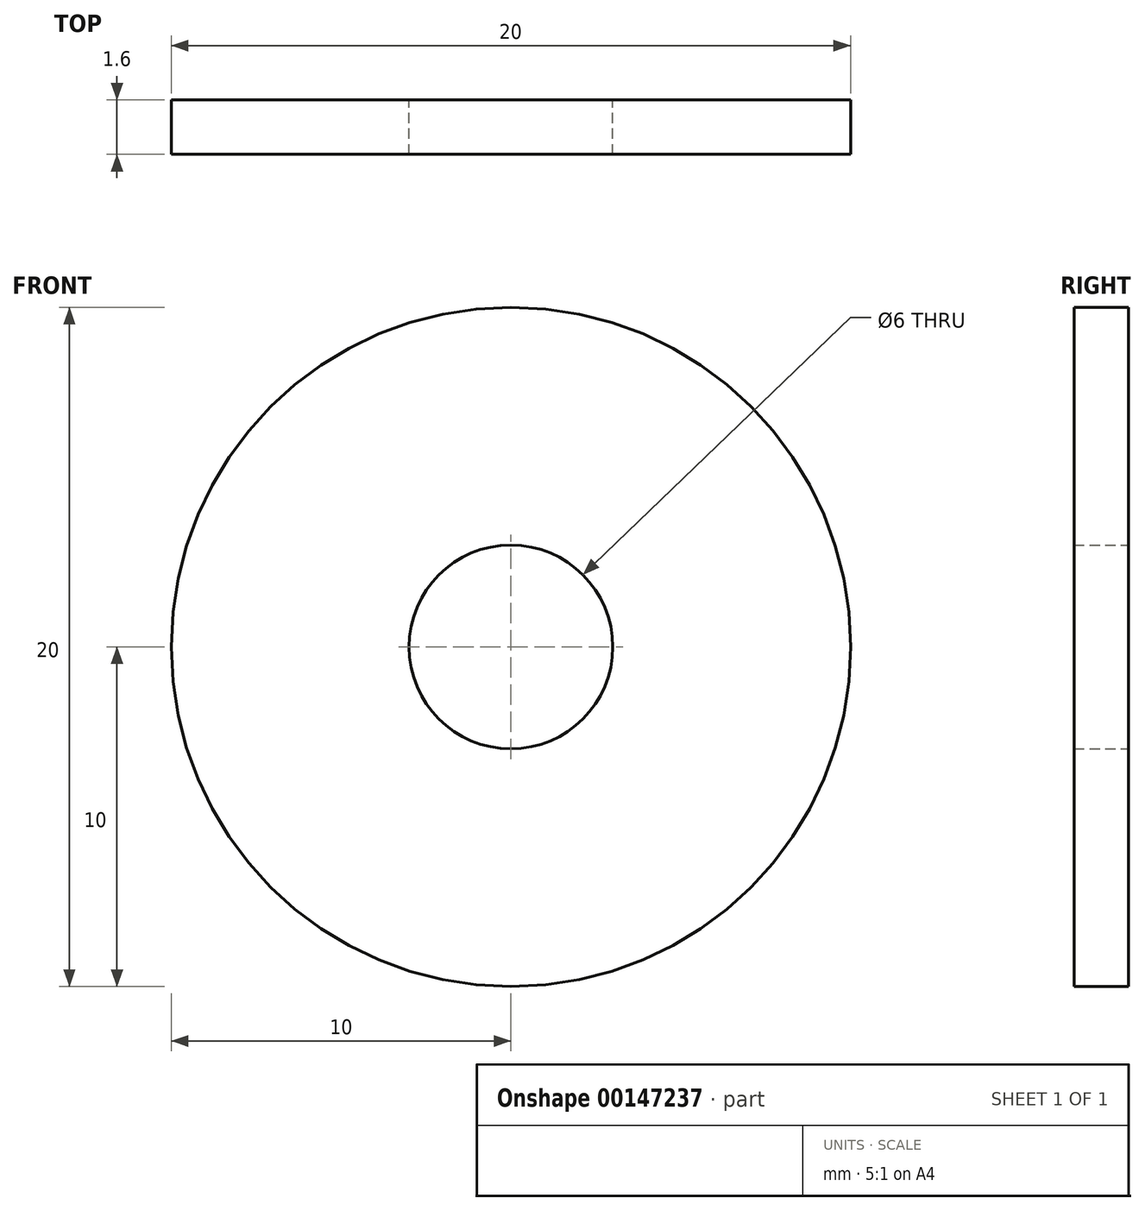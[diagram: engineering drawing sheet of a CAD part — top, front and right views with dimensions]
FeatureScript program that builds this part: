
annotation { "Feature Type Name" : "Feature", "Feature Type Description" : "" }
export const myFeature = defineFeature(function(context is Context, id is Id, definition is map)
    precondition{}
    {
        {
            var Q0;
            Q0=qCreatedBy(makeId("Front.planeOp"),FACE);
            var sketch = newSketch(context, id + "F0", { "sketchPlane" : qUnion([Q0])});
            skCircle(sketch, "E0", {"center": v(0, 0) * mm, "radius": 10 * mm});
            skCircle(sketch, "E1", {"center": v(0, 0) * mm, "radius": 3 * mm});
            skSolve(sketch);
        }
        {
            var Q0;
            Q0 = qSketchRegion(id + "F0", true);
            extrude(context, id + "F1", {"entities" : qUnion([Q0]), "depth" : 1.6 * mm});
        }
    });
